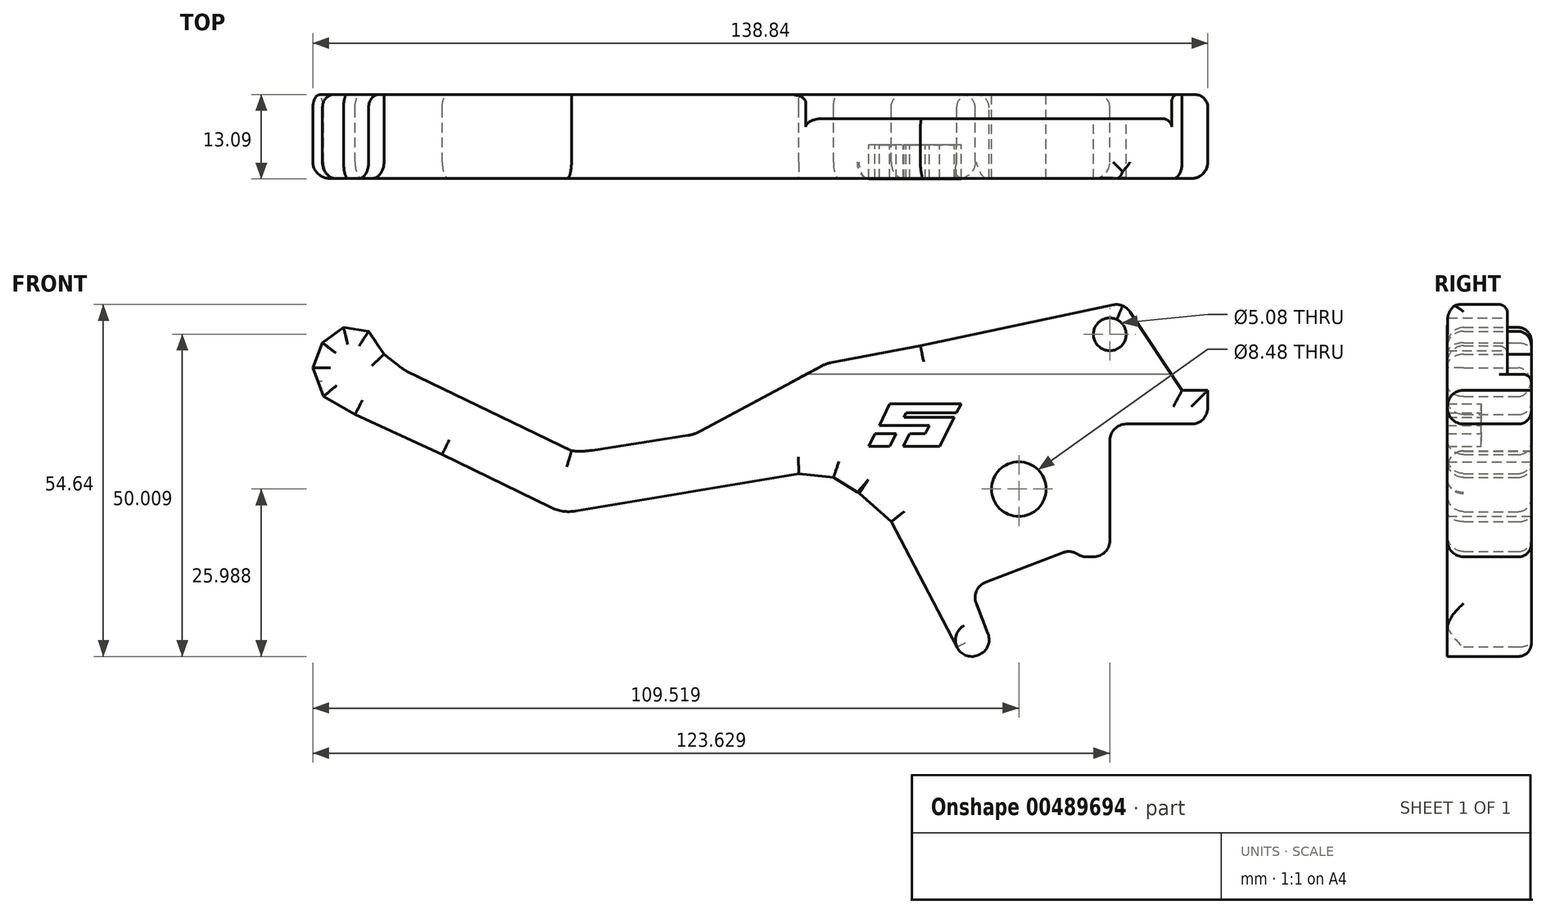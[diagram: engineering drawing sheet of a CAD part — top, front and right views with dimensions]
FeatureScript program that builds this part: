
annotation { "Feature Type Name" : "Feature", "Feature Type Description" : "" }
export const myFeature = defineFeature(function(context is Context, id is Id, definition is map)
    precondition{}
    {
        {
            var Q0;
            Q0=qCreatedBy(makeId("Front.planeOp"),FACE);
            var sketch = newSketch(context, id + "F0", { "sketchPlane" : qUnion([Q0])});
            skLineSegment(sketch, "E0", {"start": v(56.72, 12.87) * mm, "end": v(56.72, 28.41) * mm});
            skLineSegment(sketch, "E1", {"start": v(59.26, 30.95) * mm, "end": v(69.37, 30.95) * mm});
            skLineSegment(sketch, "E2", {"start": v(71.91, 33.5) * mm, "end": v(71.91, 36.2) * mm});
            skLineSegment(sketch, "E3", {"start": v(71.91, 36.2) * mm, "end": v(67.92, 36.2) * mm});
            skLineSegment(sketch, "E4", {"start": v(67.92, 36.2) * mm, "end": v(59.84, 48.37) * mm});
            skLineSegment(sketch, "E5", {"start": v(57.2, 49.45) * mm, "end": v(27.33, 43.1) * mm});
            skLineSegment(sketch, "E6", {"start": v(54.18, 10.33) * mm, "end": v(53.13, 10.33) * mm});
            skLineSegment(sketch, "E7", {"start": v(51.91, 10.63) * mm, "end": v(51.52, 10.85) * mm});
            skLineSegment(sketch, "E8", {"start": v(49.4, 10.99) * mm, "end": v(37.45, 6.4) * mm});
            skLineSegment(sketch, "E9", {"start": v(36, 3.12) * mm, "end": v(37.81, -1.63) * mm});
            skLineSegment(sketch, "E10", {"start": v(36.35, -4.9) * mm, "end": v(36.2, -4.97) * mm});
            skPoint(sketch, "E11.visualSharp", {"position": v(33.27, -6.1) * mm});
            skArc(sketch, "E11.filletArc", {"start": v(32.98, -3.66) * mm, "mid": v(34.33, -4.95) * mm, "end": v(36.2, -4.97) * mm});
            skPoint(sketch, "E12.visualSharp", {"position": v(38.72, -4) * mm});
            skArc(sketch, "E12.filletArc", {"start": v(36.35, -4.9) * mm, "mid": v(37.76, -3.57) * mm, "end": v(37.81, -1.63) * mm});
            skPoint(sketch, "E13.visualSharp", {"position": v(35.08, 5.49) * mm});
            skArc(sketch, "E13.filletArc", {"start": v(37.45, 6.4) * mm, "mid": v(36.04, 5.06) * mm, "end": v(36, 3.12) * mm});
            skPoint(sketch, "E14.visualSharp", {"position": v(50.5, 11.4) * mm});
            skArc(sketch, "E14.filletArc", {"start": v(51.52, 10.85) * mm, "mid": v(50.48, 11.15) * mm, "end": v(49.4, 10.99) * mm});
            skPoint(sketch, "E15.visualSharp", {"position": v(52.48, 10.33) * mm});
            skArc(sketch, "E15.filletArc", {"start": v(51.91, 10.63) * mm, "mid": v(52.5, 10.4) * mm, "end": v(53.13, 10.33) * mm});
            skPoint(sketch, "E16.visualSharp", {"position": v(56.72, 10.33) * mm});
            skArc(sketch, "E16.filletArc", {"start": v(54.18, 10.33) * mm, "mid": v(55.98, 11.07) * mm, "end": v(56.72, 12.87) * mm});
            skPoint(sketch, "E17.visualSharp", {"position": v(58.88, 49.8) * mm});
            skArc(sketch, "E17.filletArc", {"start": v(59.84, 48.37) * mm, "mid": v(58.68, 49.32) * mm, "end": v(57.2, 49.45) * mm});
            skPoint(sketch, "E18.visualSharp", {"position": v(71.91, 30.95) * mm});
            skArc(sketch, "E18.filletArc", {"start": v(69.37, 30.95) * mm, "mid": v(71.17, 31.7) * mm, "end": v(71.91, 33.5) * mm});
            skPoint(sketch, "E19.visualSharp", {"position": v(56.72, 30.95) * mm});
            skArc(sketch, "E19.filletArc", {"start": v(59.26, 30.95) * mm, "mid": v(57.47, 30.2) * mm, "end": v(56.72, 28.41) * mm});
            skLineSegment(sketch, "E20", {"start": v(27.33, 43.1) * mm, "end": v(13.56, 40.49) * mm});
            skLineSegment(sketch, "E21", {"start": v(-8.78, 29.18) * mm, "end": v(-23.55, 26.88) * mm});
            skLineSegment(sketch, "E22", {"start": v(-46.86, 26.2) * mm, "end": v(-30, 18) * mm});
            skLineSegment(sketch, "E23", {"start": v(-26.16, 17.44) * mm, "end": v(-4.03, 21.16) * mm});
            skLineSegment(sketch, "E24", {"start": v(-46.86, 26.2) * mm, "end": v(-60.39, 32.43) * mm});
            skLineSegment(sketch, "E25", {"start": v(-6.74, 29.87) * mm, "end": v(11.73, 39.84) * mm});
            skPoint(sketch, "E26.visualSharp", {"position": v(-27.02, 26.34) * mm});
            skArc(sketch, "E26.filletArc", {"start": v(-26.8, 26.8) * mm, "mid": v(-25.17, 26.73) * mm, "end": v(-23.55, 26.88) * mm});
            skPoint(sketch, "E27.visualSharp", {"position": v(-7.7, 29.35) * mm});
            skArc(sketch, "E27.filletArc", {"start": v(-8.78, 29.18) * mm, "mid": v(-7.73, 29.44) * mm, "end": v(-6.74, 29.87) * mm});
            skPoint(sketch, "E28.visualSharp", {"position": v(12.6, 40.3) * mm});
            skArc(sketch, "E28.filletArc", {"start": v(13.56, 40.49) * mm, "mid": v(12.62, 40.23) * mm, "end": v(11.73, 39.84) * mm});
            skPoint(sketch, "E29.visualSharp", {"position": v(5.88, 31.34) * mm});
            skPoint(sketch, "E30.visualSharp", {"position": v(0, 17.76) * mm});
            skPoint(sketch, "E31.visualSharp", {"position": v(-28.17, 17.1) * mm});
            skArc(sketch, "E31.filletArc", {"start": v(-30, 18) * mm, "mid": v(-28.12, 17.42) * mm, "end": v(-26.16, 17.44) * mm});
            skLineSegment(sketch, "E32", {"start": v(-26.8, 26.8) * mm, "end": v(-52.3, 39.13) * mm});
            skLineSegment(sketch, "E33", {"start": v(-53.2, 39.69) * mm, "end": v(-55.89, 41.78) * mm});
            skPoint(sketch, "E34.visualSharp", {"position": v(-52.77, 39.36) * mm});
            skArc(sketch, "E34.filletArc", {"start": v(-53.2, 39.69) * mm, "mid": v(-52.76, 39.39) * mm, "end": v(-52.3, 39.13) * mm});
            skLineSegment(sketch, "E35", {"start": v(-4.03, 21.16) * mm, "end": v(8.46, 23.26) * mm});
            skPoint(sketch, "E36.visualSharp", {"position": v(-4.03, 21.16) * mm});
            skLineSegment(sketch, "E37.0", {"start": v(-66.93, 39.69) * mm, "end": v(-65.29, 35.21) * mm});
            skLineSegment(sketch, "E37.1", {"start": v(-65.44, 43.57) * mm, "end": v(-66.93, 39.69) * mm});
            skLineSegment(sketch, "E37.2", {"start": v(-62.16, 45.95) * mm, "end": v(-65.44, 43.57) * mm});
            skLineSegment(sketch, "E37.3", {"start": v(-58.28, 45.36) * mm, "end": v(-62.16, 45.95) * mm});
            skLineSegment(sketch, "E37.4", {"start": v(-55.89, 41.78) * mm, "end": v(-58.28, 45.36) * mm});
            skLineSegment(sketch, "E37.8", {"start": v(-65.29, 35.21) * mm, "end": v(-60.39, 32.43) * mm});
            skCircle(sketch, "E38", {"center": v(56.7, 44.88) * mm, "radius": 2.54 * mm});
            skCircle(sketch, "E39", {"center": v(42.59, 20.86) * mm, "radius": 4.24 * mm});
            skLineSegment(sketch, "E40", {"start": v(8.46, 23.26) * mm, "end": v(13.83, 22.66) * mm});
            skLineSegment(sketch, "E41", {"start": v(13.83, 22.66) * mm, "end": v(17.71, 20.27) * mm});
            skLineSegment(sketch, "E42", {"start": v(17.71, 20.27) * mm, "end": v(22.8, 15.78) * mm});
            skLineSegment(sketch, "E43", {"start": v(32.98, -3.66) * mm, "end": v(22.8, 15.78) * mm});
            skSolve(sketch);
        }
        {
            var Q0;
            Q0=makeQuery(id+"F0.imprint","IMPRINT",FACE,{"disambiguationData":[TD([[makeQuery(id+"F0.imprint","IMPRINT",EDGE,{"derivedFrom":sQuery(id+"F0.wireOp",EDGE,"E0")}),1.0]])]});
            extrude(context, id + "F1", {"entities" : qUnion([Q0]), "depth" : 13.03 * mm});
        }
        {
            var Q0;
            Q0=makeQuery(id+"F1.opExtrude","CAP_EDGE",EDGE,{"disambiguationData":[OSD([sQuery(id+"F0.wireOp",EDGE,"E20")])],"isStart":false});
            var Q1;
            Q1=makeQuery(id+"F1.opExtrude","CAP_EDGE",EDGE,{"disambiguationData":[OSD([sQuery(id+"F0.wireOp",EDGE,"E5")])],"isStart":false});
            var Q2;
            Q2=makeQuery(id+"F1.opExtrude","CAP_EDGE",EDGE,{"disambiguationData":[OSD([sQuery(id+"F0.wireOp",EDGE,"E25")])],"isStart":false});
            var Q3;
            Q3=makeQuery(id+"F1.opExtrude","CAP_EDGE",EDGE,{"disambiguationData":[OSD([sQuery(id+"F0.wireOp",EDGE,"E21")])],"isStart":false});
            var Q4;
            Q4=makeQuery(id+"F1.opExtrude","CAP_EDGE",EDGE,{"disambiguationData":[OSD([sQuery(id+"F0.wireOp",EDGE,"E26.filletArc")])],"isStart":false});
            var Q5;
            Q5=makeQuery(id+"F1.opExtrude","CAP_EDGE",EDGE,{"disambiguationData":[OSD([sQuery(id+"F0.wireOp",EDGE,"E32")])],"isStart":false});
            var Q6;
            Q6=makeQuery(id+"F1.opExtrude","CAP_EDGE",EDGE,{"disambiguationData":[OSD([sQuery(id+"F0.wireOp",EDGE,"E33")])],"isStart":false});
            var Q7;
            Q7=makeQuery(id+"F1.opExtrude","CAP_EDGE",EDGE,{"disambiguationData":[OSD([sQuery(id+"F0.wireOp",EDGE,"E37.4")])],"isStart":false});
            var Q8;
            Q8=makeQuery(id+"F1.opExtrude","CAP_EDGE",EDGE,{"disambiguationData":[OSD([sQuery(id+"F0.wireOp",EDGE,"E37.3")])],"isStart":false});
            var Q9;
            Q9=makeQuery(id+"F1.opExtrude","CAP_EDGE",EDGE,{"disambiguationData":[OSD([sQuery(id+"F0.wireOp",EDGE,"E37.2")])],"isStart":false});
            var Q10;
            Q10=makeQuery(id+"F1.opExtrude","CAP_EDGE",EDGE,{"disambiguationData":[OSD([sQuery(id+"F0.wireOp",EDGE,"E37.1")])],"isStart":false});
            var Q11;
            Q11=makeQuery(id+"F1.opExtrude","CAP_EDGE",EDGE,{"disambiguationData":[OSD([sQuery(id+"F0.wireOp",EDGE,"E37.0")])],"isStart":false});
            var Q12;
            Q12=makeQuery(id+"F1.opExtrude","CAP_EDGE",EDGE,{"disambiguationData":[OSD([sQuery(id+"F0.wireOp",EDGE,"E37.8")])],"isStart":false});
            var Q13;
            Q13=makeQuery(id+"F1.opExtrude","CAP_EDGE",EDGE,{"disambiguationData":[OSD([sQuery(id+"F0.wireOp",EDGE,"E24")])],"isStart":false});
            var Q14;
            Q14=makeQuery(id+"F1.opExtrude","CAP_EDGE",EDGE,{"disambiguationData":[OSD([sQuery(id+"F0.wireOp",EDGE,"E22")])],"isStart":false});
            var Q15;
            Q15=makeQuery(id+"F1.opExtrude","CAP_EDGE",EDGE,{"disambiguationData":[OSD([sQuery(id+"F0.wireOp",EDGE,"E23"),sQuery(id+"F0.wireOp",EDGE,"E35")])],"isStart":false});
            var Q16;
            Q16=makeQuery(id+"F1.opExtrude","CAP_EDGE",EDGE,{"disambiguationData":[OSD([sQuery(id+"F0.wireOp",EDGE,"E40")])],"isStart":false});
            var Q17;
            Q17=makeQuery(id+"F1.opExtrude","CAP_EDGE",EDGE,{"disambiguationData":[OSD([sQuery(id+"F0.wireOp",EDGE,"E41")])],"isStart":false});
            var Q18;
            Q18=makeQuery(id+"F1.opExtrude","CAP_EDGE",EDGE,{"disambiguationData":[OSD([sQuery(id+"F0.wireOp",EDGE,"E43")])],"isStart":false});
            var Q19;
            Q19=makeQuery(id+"F1.opExtrude","CAP_EDGE",EDGE,{"disambiguationData":[OSD([sQuery(id+"F0.wireOp",EDGE,"E16.filletArc")])],"isStart":false});
            var Q20;
            Q20=makeQuery(id+"F1.opExtrude","CAP_EDGE",EDGE,{"disambiguationData":[OSD([sQuery(id+"F0.wireOp",EDGE,"E14.filletArc")])],"isStart":false});
            var Q21;
            Q21=makeQuery(id+"F1.opExtrude","CAP_EDGE",EDGE,{"disambiguationData":[OSD([sQuery(id+"F0.wireOp",EDGE,"E7")])],"isStart":false});
            var Q22;
            Q22=makeQuery(id+"F1.opExtrude","CAP_EDGE",EDGE,{"disambiguationData":[OSD([sQuery(id+"F0.wireOp",EDGE,"E15.filletArc")])],"isStart":false});
            var Q23;
            Q23=makeQuery(id+"F1.opExtrude","CAP_EDGE",EDGE,{"disambiguationData":[OSD([sQuery(id+"F0.wireOp",EDGE,"E6")])],"isStart":false});
            var Q24;
            Q24=makeQuery(id+"F1.opExtrude","CAP_EDGE",EDGE,{"disambiguationData":[OSD([sQuery(id+"F0.wireOp",EDGE,"E0")])],"isStart":false});
            var Q25;
            Q25=makeQuery(id+"F1.opExtrude","CAP_EDGE",EDGE,{"disambiguationData":[OSD([sQuery(id+"F0.wireOp",EDGE,"E19.filletArc")])],"isStart":false});
            var Q26;
            Q26=makeQuery(id+"F1.opExtrude","CAP_EDGE",EDGE,{"disambiguationData":[OSD([sQuery(id+"F0.wireOp",EDGE,"E1")])],"isStart":false});
            var Q27;
            Q27=makeQuery(id+"F1.opExtrude","CAP_EDGE",EDGE,{"disambiguationData":[OSD([sQuery(id+"F0.wireOp",EDGE,"E2")])],"isStart":false});
            var Q28;
            Q28=makeQuery(id+"F1.opExtrude","CAP_EDGE",EDGE,{"disambiguationData":[OSD([sQuery(id+"F0.wireOp",EDGE,"E4")])],"isStart":false});
            var Q29;
            Q29=makeQuery(id+"F1.opExtrude","CAP_EDGE",EDGE,{"disambiguationData":[OSD([sQuery(id+"F0.wireOp",EDGE,"E3")])],"isStart":false});
            var Q30;
            Q30=makeQuery(id+"F1.opExtrude","CAP_EDGE",EDGE,{"disambiguationData":[OSD([sQuery(id+"F0.wireOp",EDGE,"E42")])],"isStart":false});
            var Q31;
            Q31=makeQuery(id+"F1.opExtrude","CAP_EDGE",EDGE,{"disambiguationData":[OSD([sQuery(id+"F0.wireOp",EDGE,"E27.filletArc")])],"isStart":false});
            var Q32;
            Q32=makeQuery(id+"F1.opExtrude","CAP_EDGE",EDGE,{"disambiguationData":[OSD([sQuery(id+"F0.wireOp",EDGE,"E31.filletArc")])],"isStart":false});
            var Q33;
            Q33=makeQuery(id+"F1.opExtrude","CAP_EDGE",EDGE,{"disambiguationData":[OSD([sQuery(id+"F0.wireOp",EDGE,"E28.filletArc")])],"isStart":false});
            var Q34;
            Q34=makeQuery(id+"F1.opExtrude","CAP_EDGE",EDGE,{"disambiguationData":[OSD([sQuery(id+"F0.wireOp",EDGE,"E34.filletArc")])],"isStart":false});
            var Q35;
            Q35=makeQuery(id+"F1.opExtrude","CAP_EDGE",EDGE,{"disambiguationData":[OSD([sQuery(id+"F0.wireOp",EDGE,"E8")])],"isStart":false});
            var Q36;
            Q36=makeQuery(id+"F1.opExtrude","CAP_EDGE",EDGE,{"disambiguationData":[OSD([sQuery(id+"F0.wireOp",EDGE,"E13.filletArc")])],"isStart":false});
            fillet(context, id + "F2", {"entities" : qUnion([Q0, Q1, Q2, Q3, Q4, Q5, Q6, Q7, Q8, Q9, Q10, Q11, Q12, Q13, Q14, Q15, Q16, Q17, Q18, Q19, Q20, Q21, Q22, Q23, Q24, Q25, Q26, Q27, Q28, Q29, Q30, Q31, Q32, Q33, Q34, Q35, Q36]), "radius" : 2.54 * mm, "allowEdgeOverflow" : false});
        }
        {
            var Q0;
            Q0=qCreatedBy(makeId("Right.planeOp"),FACE);
            var sketch = newSketch(context, id + "F3", { "sketchPlane" : qUnion([Q0])});
            skLineSegment(sketch, "E44.bottom", {"start": v(-3.73, 52.03) * mm, "end": v(1.34, 52.03) * mm});
            skLineSegment(sketch, "E44.top", {"start": v(-3.73, 38.66) * mm, "end": v(1.34, 38.66) * mm});
            skLineSegment(sketch, "E44.left", {"start": v(-3.73, 52.03) * mm, "end": v(-3.73, 38.66) * mm});
            skLineSegment(sketch, "E44.right", {"start": v(1.34, 52.03) * mm, "end": v(1.34, 38.66) * mm});
            skSolve(sketch);
        }
        {
            var Q0;
            Q0=makeQuery(id+"F3.imprint","IMPRINT",FACE,{"disambiguationData":[TD([[makeQuery(id+"F3.imprint","IMPRINT",EDGE,{"derivedFrom":sQuery(id+"F3.wireOp",EDGE,"E44.bottom")}),-1.0]])]});
            extrude(context, id + "F4", {"entities" : qUnion([Q0]), "operationType" : NewBodyOperationType.REMOVE, "endBound" : BoundingType.THROUGH_ALL, "depth" : 25.4 * mm});
        }
        {
            var Q0;
            Q0=makeQuery(id+"F4.boolean.opBoolean","INTERSECT",EDGE,{"derivedFrom":[makeQuery(id+"F1.opExtrude","CAP_FACE",FACE,{"disambiguationData":[OSD([sQuery(id+"F0.wireOp",EDGE,"E0"),sQuery(id+"F0.wireOp",EDGE,"E1"),sQuery(id+"F0.wireOp",EDGE,"E2"),sQuery(id+"F0.wireOp",EDGE,"E3"),sQuery(id+"F0.wireOp",EDGE,"E4"),sQuery(id+"F0.wireOp",EDGE,"E5"),sQuery(id+"F0.wireOp",EDGE,"E6"),sQuery(id+"F0.wireOp",EDGE,"E7"),sQuery(id+"F0.wireOp",EDGE,"E8"),sQuery(id+"F0.wireOp",EDGE,"E9"),sQuery(id+"F0.wireOp",EDGE,"E10"),sQuery(id+"F0.wireOp",EDGE,"E11.filletArc"),sQuery(id+"F0.wireOp",EDGE,"E12.filletArc"),sQuery(id+"F0.wireOp",EDGE,"E13.filletArc"),sQuery(id+"F0.wireOp",EDGE,"E14.filletArc"),sQuery(id+"F0.wireOp",EDGE,"E15.filletArc"),sQuery(id+"F0.wireOp",EDGE,"E16.filletArc"),sQuery(id+"F0.wireOp",EDGE,"E17.filletArc"),sQuery(id+"F0.wireOp",EDGE,"E18.filletArc"),sQuery(id+"F0.wireOp",EDGE,"E19.filletArc"),sQuery(id+"F0.wireOp",EDGE,"E20"),sQuery(id+"F0.wireOp",EDGE,"E21"),sQuery(id+"F0.wireOp",EDGE,"E22"),sQuery(id+"F0.wireOp",EDGE,"E23"),sQuery(id+"F0.wireOp",EDGE,"E24"),sQuery(id+"F0.wireOp",EDGE,"E25"),sQuery(id+"F0.wireOp",EDGE,"E26.filletArc"),sQuery(id+"F0.wireOp",EDGE,"E27.filletArc"),sQuery(id+"F0.wireOp",EDGE,"E28.filletArc"),sQuery(id+"F0.wireOp",EDGE,"E31.filletArc"),sQuery(id+"F0.wireOp",EDGE,"E32"),sQuery(id+"F0.wireOp",EDGE,"E33"),sQuery(id+"F0.wireOp",EDGE,"E34.filletArc"),sQuery(id+"F0.wireOp",EDGE,"E35"),sQuery(id+"F0.wireOp",EDGE,"E37.0"),sQuery(id+"F0.wireOp",EDGE,"E37.1"),sQuery(id+"F0.wireOp",EDGE,"E37.2"),sQuery(id+"F0.wireOp",EDGE,"E37.3"),sQuery(id+"F0.wireOp",EDGE,"E37.4"),sQuery(id+"F0.wireOp",EDGE,"E37.8"),sQuery(id+"F0.wireOp",EDGE,"E38"),sQuery(id+"F0.wireOp",EDGE,"E39"),sQuery(id+"F0.wireOp",EDGE,"E40"),sQuery(id+"F0.wireOp",EDGE,"E41"),sQuery(id+"F0.wireOp",EDGE,"E42"),sQuery(id+"F0.wireOp",EDGE,"E43")])],"isStart":true}),makeQuery(id+"F4.opExtrude","SWEPT_FACE",FACE,{"disambiguationData":[OSD([sQuery(id+"F3.wireOp",EDGE,"E44.top")])]})]});
            var Q1;
            Q1=makeQuery(id+"F4.boolean.opBoolean","INTERSECT",EDGE,{"derivedFrom":[makeQuery(id+"F1.opExtrude","SWEPT_FACE",FACE,{"disambiguationData":[OSD([sQuery(id+"F0.wireOp",EDGE,"E5")])]}),makeQuery(id+"F4.opExtrude","SWEPT_FACE",FACE,{"disambiguationData":[OSD([sQuery(id+"F3.wireOp",EDGE,"E44.left")])]})]});
            var Q2;
            Q2=makeQuery(id+"F4.boolean.opBoolean","INTERSECT",EDGE,{"derivedFrom":[makeQuery(id+"F1.opExtrude","SWEPT_FACE",FACE,{"disambiguationData":[OSD([sQuery(id+"F0.wireOp",EDGE,"E20")])]}),makeQuery(id+"F4.opExtrude","SWEPT_FACE",FACE,{"disambiguationData":[OSD([sQuery(id+"F3.wireOp",EDGE,"E44.left")])]})]});
            fillet(context, id + "F5", {"entities" : qUnion([Q0, Q1, Q2]), "radius" : 1.27 * mm, "tangentPropagation" : true, "allowEdgeOverflow" : false});
        }
        {
            var Q0;
            Q0=makeQuery(id+"F1.opExtrude","CAP_EDGE",EDGE,{"disambiguationData":[OSD([sQuery(id+"F0.wireOp",EDGE,"E37.3")])],"isStart":true});
            var Q1;
            Q1=makeQuery(id+"F1.opExtrude","CAP_EDGE",EDGE,{"disambiguationData":[OSD([sQuery(id+"F0.wireOp",EDGE,"E37.1")])],"isStart":true});
            var Q2;
            Q2=makeQuery(id+"F1.opExtrude","CAP_EDGE",EDGE,{"disambiguationData":[OSD([sQuery(id+"F0.wireOp",EDGE,"E37.2")])],"isStart":true});
            var Q3;
            Q3=makeQuery(id+"F1.opExtrude","CAP_EDGE",EDGE,{"disambiguationData":[OSD([sQuery(id+"F0.wireOp",EDGE,"E37.8")])],"isStart":true});
            var Q4;
            Q4=makeQuery(id+"F1.opExtrude","CAP_EDGE",EDGE,{"disambiguationData":[OSD([sQuery(id+"F0.wireOp",EDGE,"E24")])],"isStart":true});
            var Q5;
            Q5=makeQuery(id+"F1.opExtrude","CAP_EDGE",EDGE,{"disambiguationData":[OSD([sQuery(id+"F0.wireOp",EDGE,"E22")])],"isStart":true});
            var Q6;
            Q6=makeQuery(id+"F1.opExtrude","CAP_EDGE",EDGE,{"disambiguationData":[OSD([sQuery(id+"F0.wireOp",EDGE,"E23"),sQuery(id+"F0.wireOp",EDGE,"E35")])],"isStart":true});
            var Q7;
            Q7=makeQuery(id+"F1.opExtrude","CAP_EDGE",EDGE,{"disambiguationData":[OSD([sQuery(id+"F0.wireOp",EDGE,"E31.filletArc")])],"isStart":true});
            var Q8;
            Q8=makeQuery(id+"F1.opExtrude","CAP_EDGE",EDGE,{"disambiguationData":[OSD([sQuery(id+"F0.wireOp",EDGE,"E40")])],"isStart":true});
            var Q9;
            Q9=makeQuery(id+"F1.opExtrude","CAP_EDGE",EDGE,{"disambiguationData":[OSD([sQuery(id+"F0.wireOp",EDGE,"E41")])],"isStart":true});
            var Q10;
            Q10=makeQuery(id+"F1.opExtrude","CAP_EDGE",EDGE,{"disambiguationData":[OSD([sQuery(id+"F0.wireOp",EDGE,"E42")])],"isStart":true});
            var Q11;
            Q11=makeQuery(id+"F1.opExtrude","CAP_EDGE",EDGE,{"disambiguationData":[OSD([sQuery(id+"F0.wireOp",EDGE,"E9")])],"isStart":true});
            var Q12;
            Q12=makeQuery(id+"F1.opExtrude","CAP_EDGE",EDGE,{"disambiguationData":[OSD([sQuery(id+"F0.wireOp",EDGE,"E13.filletArc")])],"isStart":true});
            var Q13;
            Q13=makeQuery(id+"F1.opExtrude","CAP_EDGE",EDGE,{"disambiguationData":[OSD([sQuery(id+"F0.wireOp",EDGE,"E8")])],"isStart":true});
            var Q14;
            Q14=makeQuery(id+"F1.opExtrude","CAP_EDGE",EDGE,{"disambiguationData":[OSD([sQuery(id+"F0.wireOp",EDGE,"E14.filletArc")])],"isStart":true});
            var Q15;
            Q15=makeQuery(id+"F1.opExtrude","CAP_EDGE",EDGE,{"disambiguationData":[OSD([sQuery(id+"F0.wireOp",EDGE,"E7")])],"isStart":true});
            var Q16;
            Q16=makeQuery(id+"F1.opExtrude","CAP_EDGE",EDGE,{"disambiguationData":[OSD([sQuery(id+"F0.wireOp",EDGE,"E6")])],"isStart":true});
            var Q17;
            Q17=makeQuery(id+"F1.opExtrude","CAP_EDGE",EDGE,{"disambiguationData":[OSD([sQuery(id+"F0.wireOp",EDGE,"E15.filletArc")])],"isStart":true});
            var Q18;
            Q18=makeQuery(id+"F1.opExtrude","CAP_EDGE",EDGE,{"disambiguationData":[OSD([sQuery(id+"F0.wireOp",EDGE,"E11.filletArc")])],"isStart":true});
            var Q19;
            Q19=makeQuery(id+"F1.opExtrude","CAP_EDGE",EDGE,{"disambiguationData":[OSD([sQuery(id+"F0.wireOp",EDGE,"E16.filletArc")])],"isStart":true});
            var Q20;
            Q20=makeQuery(id+"F1.opExtrude","CAP_EDGE",EDGE,{"disambiguationData":[OSD([sQuery(id+"F0.wireOp",EDGE,"E0")])],"isStart":true});
            var Q21;
            Q21=makeQuery(id+"F1.opExtrude","CAP_EDGE",EDGE,{"disambiguationData":[OSD([sQuery(id+"F0.wireOp",EDGE,"E19.filletArc")])],"isStart":true});
            var Q22;
            Q22=makeQuery(id+"F1.opExtrude","CAP_EDGE",EDGE,{"disambiguationData":[OSD([sQuery(id+"F0.wireOp",EDGE,"E1")])],"isStart":true});
            var Q23;
            Q23=makeQuery(id+"F1.opExtrude","CAP_EDGE",EDGE,{"disambiguationData":[OSD([sQuery(id+"F0.wireOp",EDGE,"E18.filletArc")])],"isStart":true});
            var Q24;
            Q24=makeQuery(id+"F2.opFillet","BLEND_EDGE",EDGE,{"blendedFrom":[makeQuery(id+"F1.opExtrude","CAP_EDGE",EDGE,{"disambiguationData":[OSD([sQuery(id+"F0.wireOp",EDGE,"E41")])],"isStart":false}),makeQuery(id+"F1.opExtrude","CAP_EDGE",EDGE,{"disambiguationData":[OSD([sQuery(id+"F0.wireOp",EDGE,"E42")])],"isStart":false})],"blendedInto":[]});
            var Q25;
            Q25=makeQuery(id+"F1.opExtrude","CAP_EDGE",EDGE,{"disambiguationData":[OSD([sQuery(id+"F0.wireOp",EDGE,"E43")])],"isStart":true});
            fillet(context, id + "F6", {"entities" : qUnion([Q0, Q1, Q2, Q3, Q4, Q5, Q6, Q7, Q8, Q9, Q10, Q11, Q12, Q13, Q14, Q15, Q16, Q17, Q18, Q19, Q20, Q21, Q22, Q23, Q24, Q25]), "radius" : 2.03 * mm, "tangentPropagation" : true, "allowEdgeOverflow" : false});
        }
        {
            var Q0;
            Q0=qCreatedBy(makeId("Front.planeOp"),FACE);
            var sketch = newSketch(context, id + "F7", { "sketchPlane" : qUnion([Q0])});
            skLineSegment(sketch, "E45", {"start": v(-34.99, 78.38) * mm, "end": v(-62.52, 78.38) * mm, "construction": true});
            skLineSegment(sketch, "E46", {"start": v(-62.52, 78.38) * mm, "end": v(-54.32, 94.9) * mm, "construction": true});
            skLineSegment(sketch, "E47", {"start": v(-26.67, 94.9) * mm, "end": v(-34.99, 78.38) * mm, "construction": true});
            skLineSegment(sketch, "E48", {"start": v(-34.99, 78.38) * mm, "end": v(-49.16, 78.38) * mm});
            skLineSegment(sketch, "E49", {"start": v(-49.16, 78.38) * mm, "end": v(-46.64, 83.36) * mm});
            skLineSegment(sketch, "E50", {"start": v(-46.64, 83.36) * mm, "end": v(-40.58, 83.36) * mm});
            skLineSegment(sketch, "E51", {"start": v(-40.58, 83.36) * mm, "end": v(-38.99, 86.52) * mm});
            skLineSegment(sketch, "E52", {"start": v(-38.99, 86.52) * mm, "end": v(-58.42, 86.52) * mm});
            skPoint(sketch, "E52.endSnap0", {"position": v(-58.42, 86.63) * mm});
            skLineSegment(sketch, "E53", {"start": v(-58.42, 86.52) * mm, "end": v(-54.32, 94.9) * mm});
            skLineSegment(sketch, "E54", {"start": v(-26.67, 94.9) * mm, "end": v(-28.44, 91.37) * mm});
            skLineSegment(sketch, "E55", {"start": v(-28.44, 91.37) * mm, "end": v(-48.02, 91.37) * mm});
            skLineSegment(sketch, "E56", {"start": v(-48.02, 91.37) * mm, "end": v(-48.82, 89.77) * mm});
            skLineSegment(sketch, "E57", {"start": v(-48.82, 89.77) * mm, "end": v(-29.25, 89.77) * mm});
            skLineSegment(sketch, "E58", {"start": v(-29.25, 89.77) * mm, "end": v(-34.99, 78.38) * mm});
            skLineSegment(sketch, "E59", {"start": v(-54.32, 78.38) * mm, "end": v(-51.86, 83.32) * mm});
            skLineSegment(sketch, "E60", {"start": v(-51.86, 83.32) * mm, "end": v(-60.06, 83.32) * mm});
            skLineSegment(sketch, "E61", {"start": v(-60.06, 83.32) * mm, "end": v(-62.52, 78.38) * mm});
            skLineSegment(sketch, "E62", {"start": v(-26.67, 94.9) * mm, "end": v(-54.32, 94.9) * mm});
            skLineSegment(sketch, "E63", {"start": v(-54.32, 78.38) * mm, "end": v(-62.52, 78.38) * mm});
            skSolve(sketch);
        }
        {
            var Q0;
            Q0 = qSketchRegion(id + "F7", true);
            extrude(context, id + "F8", {"entities" : qUnion([Q0]), "depth" : 13.18 * mm});
        }
        {
            var Q0;
            Q0=makeQuery(id+"F8.opExtrude","SWEPT_BODY",BODY,{"disambiguationData":[OSD([sQuery(id+"F7.wireOp",EDGE,"E48"),sQuery(id+"F7.wireOp",EDGE,"E49"),sQuery(id+"F7.wireOp",EDGE,"E50"),sQuery(id+"F7.wireOp",EDGE,"E51"),sQuery(id+"F7.wireOp",EDGE,"E52"),sQuery(id+"F7.wireOp",EDGE,"E53"),sQuery(id+"F7.wireOp",EDGE,"E54"),sQuery(id+"F7.wireOp",EDGE,"E55"),sQuery(id+"F7.wireOp",EDGE,"E56"),sQuery(id+"F7.wireOp",EDGE,"E57"),sQuery(id+"F7.wireOp",EDGE,"E58"),sQuery(id+"F7.wireOp",EDGE,"E62")])]});
            var Q1;
            Q1=makeQuery(id+"F8.opExtrude","SWEPT_BODY",BODY,{"disambiguationData":[OSD([sQuery(id+"F7.wireOp",EDGE,"E59"),sQuery(id+"F7.wireOp",EDGE,"E60"),sQuery(id+"F7.wireOp",EDGE,"E61"),sQuery(id+"F7.wireOp",EDGE,"E63")])]});
            var Q2;
            {var subQ0=sQuery(id+"F0.wireOp",EDGE,"E42");var subQ1=sQuery(id+"F0.wireOp",EDGE,"E41");Q2=makeQuery(id+"F6.opFillet","BLEND_VERTEX",VERTEX,{"blendedFrom":[makeQuery(id+"F2.opFillet","BLEND_EDGE",EDGE,{"blendedFrom":[makeQuery(id+"F1.opExtrude","CAP_EDGE",EDGE,{"disambiguationData":[OSD([subQ1])],"isStart":false}),makeQuery(id+"F1.opExtrude","CAP_EDGE",EDGE,{"disambiguationData":[OSD([subQ0])],"isStart":false})],"blendedInto":[]}),makeQuery(id+"F2.opFillet","BLEND_FACE",FACE,{"disambiguationData":[OSD([subQ1])]}),makeQuery(id+"F2.opFillet","BLEND_FACE",FACE,{"disambiguationData":[OSD([subQ0])]}),makeQuery(id+"F1.opExtrude","CAP_FACE",FACE,{"disambiguationData":[OSD([sQuery(id+"F0.wireOp",EDGE,"E0"),sQuery(id+"F0.wireOp",EDGE,"E1"),sQuery(id+"F0.wireOp",EDGE,"E2"),sQuery(id+"F0.wireOp",EDGE,"E3"),sQuery(id+"F0.wireOp",EDGE,"E4"),sQuery(id+"F0.wireOp",EDGE,"E5"),sQuery(id+"F0.wireOp",EDGE,"E6"),sQuery(id+"F0.wireOp",EDGE,"E7"),sQuery(id+"F0.wireOp",EDGE,"E8"),sQuery(id+"F0.wireOp",EDGE,"E9"),sQuery(id+"F0.wireOp",EDGE,"E10"),sQuery(id+"F0.wireOp",EDGE,"E11.filletArc"),sQuery(id+"F0.wireOp",EDGE,"E12.filletArc"),sQuery(id+"F0.wireOp",EDGE,"E13.filletArc"),sQuery(id+"F0.wireOp",EDGE,"E14.filletArc"),sQuery(id+"F0.wireOp",EDGE,"E15.filletArc"),sQuery(id+"F0.wireOp",EDGE,"E16.filletArc"),sQuery(id+"F0.wireOp",EDGE,"E17.filletArc"),sQuery(id+"F0.wireOp",EDGE,"E18.filletArc"),sQuery(id+"F0.wireOp",EDGE,"E19.filletArc"),sQuery(id+"F0.wireOp",EDGE,"E20"),sQuery(id+"F0.wireOp",EDGE,"E21"),sQuery(id+"F0.wireOp",EDGE,"E22"),sQuery(id+"F0.wireOp",EDGE,"E23"),sQuery(id+"F0.wireOp",EDGE,"E24"),sQuery(id+"F0.wireOp",EDGE,"E25"),sQuery(id+"F0.wireOp",EDGE,"E26.filletArc"),sQuery(id+"F0.wireOp",EDGE,"E27.filletArc"),sQuery(id+"F0.wireOp",EDGE,"E28.filletArc"),sQuery(id+"F0.wireOp",EDGE,"E31.filletArc"),sQuery(id+"F0.wireOp",EDGE,"E32"),sQuery(id+"F0.wireOp",EDGE,"E33"),sQuery(id+"F0.wireOp",EDGE,"E34.filletArc"),sQuery(id+"F0.wireOp",EDGE,"E35"),sQuery(id+"F0.wireOp",EDGE,"E37.0"),sQuery(id+"F0.wireOp",EDGE,"E37.1"),sQuery(id+"F0.wireOp",EDGE,"E37.2"),sQuery(id+"F0.wireOp",EDGE,"E37.3"),sQuery(id+"F0.wireOp",EDGE,"E37.4"),sQuery(id+"F0.wireOp",EDGE,"E37.8"),sQuery(id+"F0.wireOp",EDGE,"E38"),sQuery(id+"F0.wireOp",EDGE,"E39"),sQuery(id+"F0.wireOp",EDGE,"E40"),subQ1,subQ0,sQuery(id+"F0.wireOp",EDGE,"E43")])],"isStart":false})],"blendedInto":[makeQuery(id+"F2.opFillet","BLEND_FACE",FACE,{"disambiguationData":[OSD([subQ1])]}),makeQuery(id+"F2.opFillet","BLEND_FACE",FACE,{"disambiguationData":[OSD([subQ0])]}),makeQuery(id+"F1.opExtrude","CAP_FACE",FACE,{"disambiguationData":[OSD([sQuery(id+"F0.wireOp",EDGE,"E0"),sQuery(id+"F0.wireOp",EDGE,"E1"),sQuery(id+"F0.wireOp",EDGE,"E2"),sQuery(id+"F0.wireOp",EDGE,"E3"),sQuery(id+"F0.wireOp",EDGE,"E4"),sQuery(id+"F0.wireOp",EDGE,"E5"),sQuery(id+"F0.wireOp",EDGE,"E6"),sQuery(id+"F0.wireOp",EDGE,"E7"),sQuery(id+"F0.wireOp",EDGE,"E8"),sQuery(id+"F0.wireOp",EDGE,"E9"),sQuery(id+"F0.wireOp",EDGE,"E10"),sQuery(id+"F0.wireOp",EDGE,"E11.filletArc"),sQuery(id+"F0.wireOp",EDGE,"E12.filletArc"),sQuery(id+"F0.wireOp",EDGE,"E13.filletArc"),sQuery(id+"F0.wireOp",EDGE,"E14.filletArc"),sQuery(id+"F0.wireOp",EDGE,"E15.filletArc"),sQuery(id+"F0.wireOp",EDGE,"E16.filletArc"),sQuery(id+"F0.wireOp",EDGE,"E17.filletArc"),sQuery(id+"F0.wireOp",EDGE,"E18.filletArc"),sQuery(id+"F0.wireOp",EDGE,"E19.filletArc"),sQuery(id+"F0.wireOp",EDGE,"E20"),sQuery(id+"F0.wireOp",EDGE,"E21"),sQuery(id+"F0.wireOp",EDGE,"E22"),sQuery(id+"F0.wireOp",EDGE,"E23"),sQuery(id+"F0.wireOp",EDGE,"E24"),sQuery(id+"F0.wireOp",EDGE,"E25"),sQuery(id+"F0.wireOp",EDGE,"E26.filletArc"),sQuery(id+"F0.wireOp",EDGE,"E27.filletArc"),sQuery(id+"F0.wireOp",EDGE,"E28.filletArc"),sQuery(id+"F0.wireOp",EDGE,"E31.filletArc"),sQuery(id+"F0.wireOp",EDGE,"E32"),sQuery(id+"F0.wireOp",EDGE,"E33"),sQuery(id+"F0.wireOp",EDGE,"E34.filletArc"),sQuery(id+"F0.wireOp",EDGE,"E35"),sQuery(id+"F0.wireOp",EDGE,"E37.0"),sQuery(id+"F0.wireOp",EDGE,"E37.1"),sQuery(id+"F0.wireOp",EDGE,"E37.2"),sQuery(id+"F0.wireOp",EDGE,"E37.3"),sQuery(id+"F0.wireOp",EDGE,"E37.4"),sQuery(id+"F0.wireOp",EDGE,"E37.8"),sQuery(id+"F0.wireOp",EDGE,"E38"),sQuery(id+"F0.wireOp",EDGE,"E39"),sQuery(id+"F0.wireOp",EDGE,"E40"),subQ1,subQ0,sQuery(id+"F0.wireOp",EDGE,"E43")])],"isStart":false})]});}
            transform(context, id + "F9", {"entities" : qUnion([Q0, Q1]), "transformType" : TransformType.SCALE_UNIFORMLY, "scale" : .4, "scalePoint" : qUnion([Q2]), "makeCopy" : false});
        }
        {
            var Q0;
            Q0=makeQuery(id+"F8.opExtrude","SWEPT_BODY",BODY,{"disambiguationData":[OSD([sQuery(id+"F7.wireOp",EDGE,"E48"),sQuery(id+"F7.wireOp",EDGE,"E49"),sQuery(id+"F7.wireOp",EDGE,"E50"),sQuery(id+"F7.wireOp",EDGE,"E51"),sQuery(id+"F7.wireOp",EDGE,"E52"),sQuery(id+"F7.wireOp",EDGE,"E53"),sQuery(id+"F7.wireOp",EDGE,"E54"),sQuery(id+"F7.wireOp",EDGE,"E55"),sQuery(id+"F7.wireOp",EDGE,"E56"),sQuery(id+"F7.wireOp",EDGE,"E57"),sQuery(id+"F7.wireOp",EDGE,"E58"),sQuery(id+"F7.wireOp",EDGE,"E62")])]});
            var Q1;
            Q1=makeQuery(id+"F8.opExtrude","SWEPT_BODY",BODY,{"disambiguationData":[OSD([sQuery(id+"F7.wireOp",EDGE,"E59"),sQuery(id+"F7.wireOp",EDGE,"E60"),sQuery(id+"F7.wireOp",EDGE,"E61"),sQuery(id+"F7.wireOp",EDGE,"E63")])]});
            transform(context, id + "F10", {"entities" : qUnion([Q0, Q1]), "transformType" : TransformType.TRANSLATION_3D, "dx" : 32.77 * mm, "dy" : 0 * mm, "dz" : -17.27 * mm, "makeCopy" : false});
        }
    });
